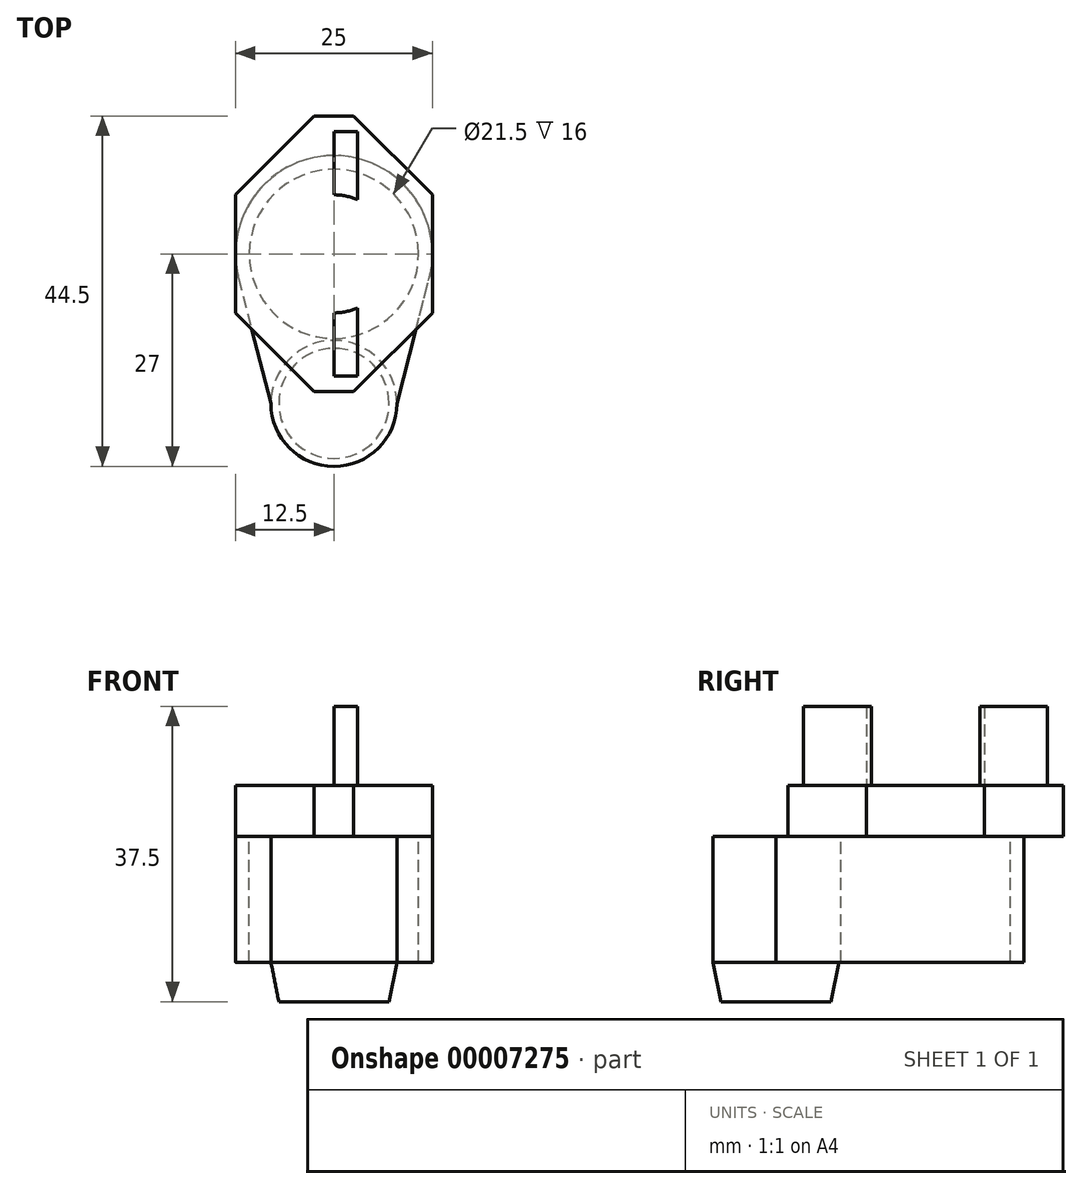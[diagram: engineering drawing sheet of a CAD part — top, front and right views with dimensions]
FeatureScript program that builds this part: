
annotation { "Feature Type Name" : "Feature", "Feature Type Description" : "" }
export const myFeature = defineFeature(function(context is Context, id is Id, definition is map)
    precondition{}
    {
        {
            var Q0;
            Q0=qCreatedBy(makeId("Top.planeOp"),FACE);
            var sketch = newSketch(context, id + "F0", { "sketchPlane" : qUnion([Q0])});
            skLineSegment(sketch, "E0.rect.bottom", {"start": v(12.5, 17.5) * mm, "end": v(-12.5, 17.5) * mm});
            skLineSegment(sketch, "E0.rect.top", {"start": v(12.5, -17.5) * mm, "end": v(-12.5, -17.5) * mm});
            skLineSegment(sketch, "E0.rect.left", {"start": v(12.5, 17.5) * mm, "end": v(12.5, -17.5) * mm});
            skLineSegment(sketch, "E0.rect.right", {"start": v(-12.5, 17.5) * mm, "end": v(-12.5, -17.5) * mm});
            skPoint(sketch, "E0.rect.middle", {"position": v(0, 0) * mm});
            skSolve(sketch);
        }
        {
            var Q0;
            Q0 = qSketchRegion(id + "F0", true);
            extrude(context, id + "F1", {"entities" : qUnion([Q0]), "depth" : 6.5 * mm});
        }
        {
            var Q0;
            Q0=makeQuery(id+"F1.opExtrude","CAP_FACE",FACE,{"disambiguationData":[OSD([sQuery(id+"F0.wireOp",EDGE,"E0.rect.bottom"),sQuery(id+"F0.wireOp",EDGE,"E0.rect.top"),sQuery(id+"F0.wireOp",EDGE,"E0.rect.left"),sQuery(id+"F0.wireOp",EDGE,"E0.rect.right")])],"isStart":false});
            var sketch = newSketch(context, id + "F2", { "sketchPlane" : qUnion([Q0])});
            skArc(sketch, "E1", {"start": v(3, 6.87) * mm, "mid": v(1.53, 7.34) * mm, "end": v(0, 7.5) * mm});
            skLineSegment(sketch, "E2", {"start": v(0, 7.5) * mm, "end": v(0, 15.5) * mm});
            skLineSegment(sketch, "E3", {"start": v(0, 15.5) * mm, "end": v(3, 15.5) * mm});
            skLineSegment(sketch, "E4", {"start": v(3, 15.5) * mm, "end": v(3, 6.87) * mm});
            skLineSegment(sketch, "E5.MirrorCS", {"start": v(3, -15.5) * mm, "end": v(3, -6.87) * mm});
            skLineSegment(sketch, "E6.MirrorCS", {"start": v(0, -15.5) * mm, "end": v(3, -15.5) * mm});
            skLineSegment(sketch, "E7.MirrorCS", {"start": v(0, -7.5) * mm, "end": v(0, -15.5) * mm});
            skArc(sketch, "E8.trimOffspring", {"start": v(0, -7.5) * mm, "mid": v(1.53, -7.34) * mm, "end": v(3, -6.87) * mm});
            skSolve(sketch);
        }
        {
            var Q0;
            Q0 = qSketchRegion(id + "F2", true);
            extrude(context, id + "F3", {"entities" : qUnion([Q0]), "operationType" : NewBodyOperationType.ADD, "depth" : 10 * mm});
        }
        {
            var Q0;
            Q0=makeQuery(id+"F1.opExtrude","CAP_FACE",FACE,{"disambiguationData":[OSD([sQuery(id+"F0.wireOp",EDGE,"E0.rect.bottom"),sQuery(id+"F0.wireOp",EDGE,"E0.rect.top"),sQuery(id+"F0.wireOp",EDGE,"E0.rect.left"),sQuery(id+"F0.wireOp",EDGE,"E0.rect.right")])],"isStart":true});
            var sketch = newSketch(context, id + "F4", { "sketchPlane" : qUnion([Q0])});
            skCircle(sketch, "E9", {"center": v(0, 0) * mm, "radius": 10.75 * mm});
            skArc(sketch, "E10", {"start": v(-12.1, 3.13) * mm, "mid": v(0, -12.5) * mm, "end": v(12.1, 3.13) * mm});
            skArc(sketch, "E11", {"start": v(8, 19) * mm, "mid": v(0, 27) * mm, "end": v(-8, 19) * mm});
            skLineSegment(sketch, "E12", {"start": v(8, 19) * mm, "end": v(12.1, 3.13) * mm});
            skLineSegment(sketch, "E13", {"start": v(-12.1, 3.13) * mm, "end": v(-8, 19) * mm});
            skSolve(sketch);
        }
        {
            var Q0;
            Q0 = qSketchRegion(id + "F4", true);
            extrude(context, id + "F5", {"entities" : qUnion([Q0]), "operationType" : NewBodyOperationType.ADD, "depth" : 16 * mm});
        }
        {
            var Q0;
            Q0=makeQuery(id+"F5.opExtrude","CAP_FACE",FACE,{"disambiguationData":[OSD([sQuery(id+"F4.wireOp",EDGE,"E9"),sQuery(id+"F4.wireOp",EDGE,"E10"),sQuery(id+"F4.wireOp",EDGE,"E11"),sQuery(id+"F4.wireOp",EDGE,"E12"),sQuery(id+"F4.wireOp",EDGE,"E13")])],"isStart":false});
            var sketch = newSketch(context, id + "F6", { "sketchPlane" : qUnion([Q0])});
            skCircle(sketch, "E14", {"center": v(0, 19) * mm, "radius": 8 * mm});
            skSolve(sketch);
        }
        {
            var Q0;
            Q0 = qSketchRegion(id + "F6", true);
            extrude(context, id + "F7", {"entities" : qUnion([Q0]), "operationType" : NewBodyOperationType.ADD, "depth" : 5 * mm});
        }
        {
            var Q0;
            Q0=makeQuery(id+"F7.opExtrude","CAP_EDGE",EDGE,{"disambiguationData":[OSD([sQuery(id+"F6.wireOp",EDGE,"E14")])],"isStart":false});
            chamfer(context, id + "F8", {"entities" : qUnion([Q0]), "chamferType" : ChamferType.TWO_OFFSETS, "width1" : 1 * mm, "oppositeDirection" : false, "width2" : 5 * mm, "tangentPropagation" : true});
        }
        {
            var Q0;
            Q0=makeQuery(id+"F1.opExtrude","SWEPT_EDGE",EDGE,{"disambiguationData":[OSD([sQuery(id+"F0.wireOp",EDGE,"E0.rect.top"),sQuery(id+"F0.wireOp",EDGE,"E0.rect.left")])]});
            var Q1;
            Q1=makeQuery(id+"F1.opExtrude","SWEPT_EDGE",EDGE,{"disambiguationData":[OSD([sQuery(id+"F0.wireOp",EDGE,"E0.rect.top"),sQuery(id+"F0.wireOp",EDGE,"E0.rect.right")])]});
            var Q2;
            Q2=makeQuery(id+"F1.opExtrude","SWEPT_EDGE",EDGE,{"disambiguationData":[OSD([sQuery(id+"F0.wireOp",EDGE,"E0.rect.bottom"),sQuery(id+"F0.wireOp",EDGE,"E0.rect.left")])]});
            var Q3;
            Q3=makeQuery(id+"F1.opExtrude","SWEPT_EDGE",EDGE,{"disambiguationData":[OSD([sQuery(id+"F0.wireOp",EDGE,"E0.rect.bottom"),sQuery(id+"F0.wireOp",EDGE,"E0.rect.right")])]});
            chamfer(context, id + "F9", {"entities" : qUnion([Q0, Q1, Q2, Q3]), "width" : 10 * mm, "tangentPropagation" : true});
        }
    });
